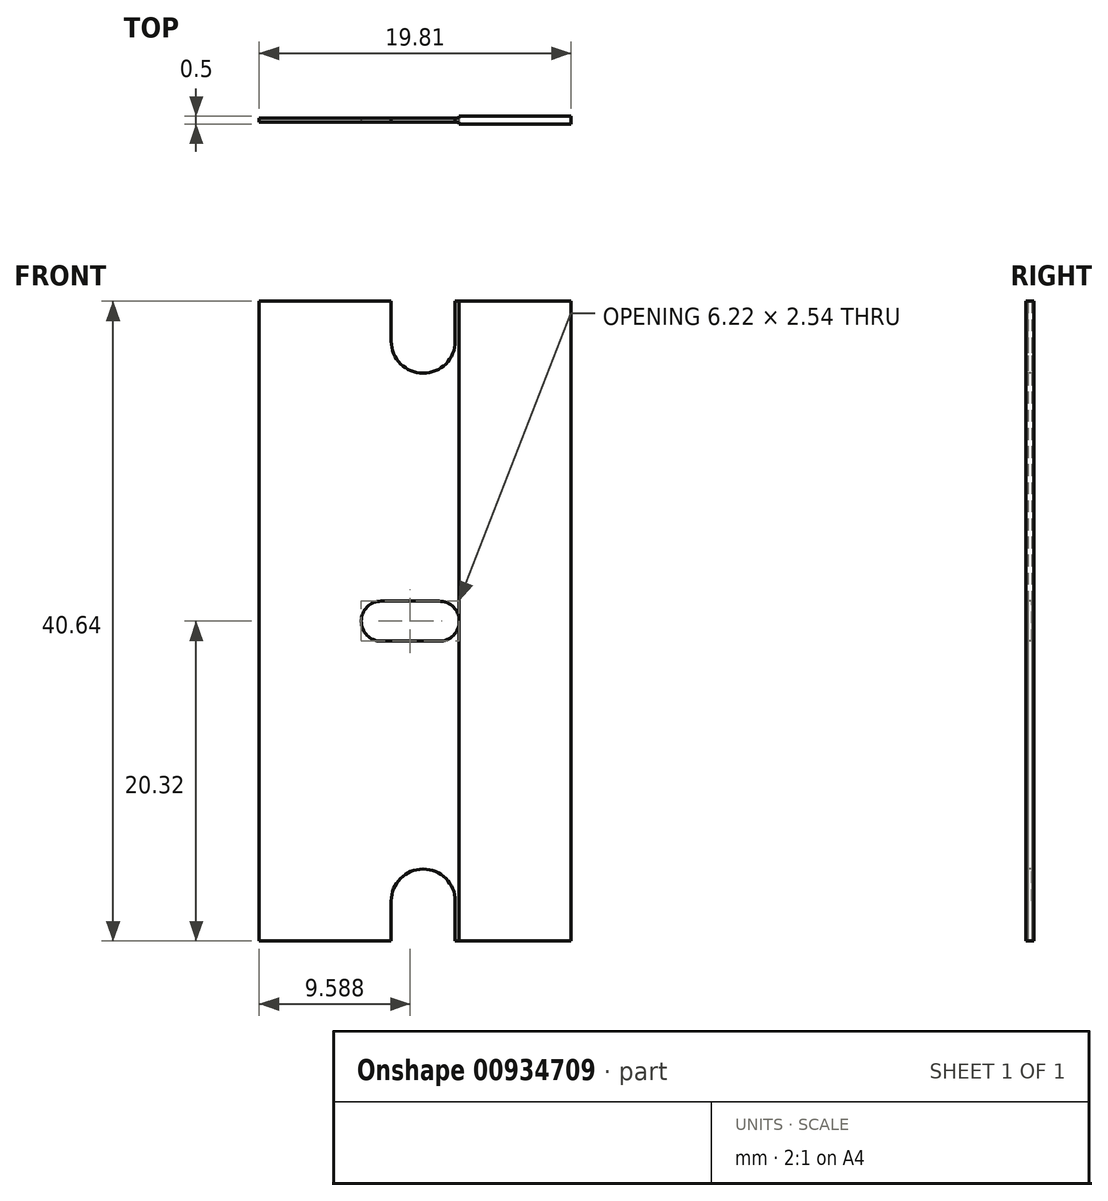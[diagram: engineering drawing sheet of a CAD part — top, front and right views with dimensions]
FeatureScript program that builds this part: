
annotation { "Feature Type Name" : "Feature", "Feature Type Description" : "" }
export const myFeature = defineFeature(function(context is Context, id is Id, definition is map)
    precondition{}
    {
        {
            var Q0;
            Q0=qCreatedBy(makeId("Top.planeOp"),FACE);
            var sketch = newSketch(context, id + "F0", { "sketchPlane" : qUnion([Q0])});
            skLineSegment(sketch, "E0", {"start": v(-12.7, 0.13) * mm, "end": v(0, 0.13) * mm});
            skLineSegment(sketch, "E1", {"start": v(0, 0.13) * mm, "end": v(0, 0.25) * mm});
            skLineSegment(sketch, "E2", {"start": v(0, 0.25) * mm, "end": v(7.11, 0.25) * mm});
            skLineSegment(sketch, "E3", {"start": v(7.11, 0.25) * mm, "end": v(7.11, -0.25) * mm});
            skLineSegment(sketch, "E4", {"start": v(7.11, -0.25) * mm, "end": v(0, -0.25) * mm});
            skLineSegment(sketch, "E5", {"start": v(0, -0.25) * mm, "end": v(0, -0.13) * mm});
            skLineSegment(sketch, "E6", {"start": v(0, -0.13) * mm, "end": v(-12.7, -0.13) * mm});
            skLineSegment(sketch, "E7", {"start": v(-12.7, -0.13) * mm, "end": v(-12.7, 0.13) * mm});
            skLineSegment(sketch, "E8", {"start": v(7.11, 0) * mm, "end": v(-12.7, 0) * mm, "construction": true});
            skSolve(sketch);
        }
        {
            var Q0;
            Q0 = qSketchRegion(id + "F0", true);
            extrude(context, id + "F1", {"entities" : qUnion([Q0]), "depth" : 40.64 * mm, "offsetDistance" : 25.4 * mm});
        }
        {
            var Q0;
            Q0=qCreatedBy(makeId("Front.planeOp"),FACE);
            var sketch = newSketch(context, id + "F2", { "sketchPlane" : qUnion([Q0])});
            skLineSegment(sketch, "E9.left", {"start": v(-4.32, 38.1) * mm, "end": v(-4.32, 40.64) * mm});
            skLineSegment(sketch, "E9.right", {"start": v(-0.25, 38.1) * mm, "end": v(-0.25, 40.64) * mm});
            skLineSegment(sketch, "E10.left", {"start": v(-4.32, 0) * mm, "end": v(-4.32, 2.54) * mm});
            skLineSegment(sketch, "E10.right", {"start": v(-0.25, 0) * mm, "end": v(-0.25, 2.54) * mm});
            skLineSegment(sketch, "E11.bottom", {"start": v(-4.95, 21.6) * mm, "end": v(-1.27, 21.6) * mm});
            skLineSegment(sketch, "E11.top", {"start": v(-4.95, 19.05) * mm, "end": v(-1.27, 19.05) * mm});
            skArc(sketch, "E12", {"start": v(-4.32, 38.1) * mm, "mid": v(-2.29, 36.07) * mm, "end": v(-0.25, 38.1) * mm});
            skArc(sketch, "E13", {"start": v(-4.95, 21.6) * mm, "mid": v(-6.22, 20.32) * mm, "end": v(-4.95, 19.05) * mm});
            skArc(sketch, "E14", {"start": v(-1.27, 21.6) * mm, "mid": v(0, 20.32) * mm, "end": v(-1.27, 19.05) * mm});
            skLineSegment(sketch, "E15", {"start": v(-4.32, 0) * mm, "end": v(-0.25, 0) * mm});
            skLineSegment(sketch, "E16", {"start": v(-4.32, 40.64) * mm, "end": v(-0.25, 40.64) * mm});
            skLineSegment(sketch, "E17", {"start": v(-13.98, 20.32) * mm, "end": v(0, 20.32) * mm, "construction": true});
            skArc(sketch, "E18", {"start": v(-4.32, 2.54) * mm, "mid": v(-2.29, 4.57) * mm, "end": v(-0.25, 2.54) * mm});
            skSolve(sketch);
        }
        {
            var Q0;
            Q0 = qSketchRegion(id + "F2", true);
            extrude(context, id + "F3", {"entities" : qUnion([Q0]), "operationType" : NewBodyOperationType.REMOVE, "endBound" : BoundingType.THROUGH_ALL, "oppositeDirection" : true, "depth" : 25.4 * mm, "offsetDistance" : 25.4 * mm, "hasSecondDirection" : true, "secondDirectionBound" : SecondDirectionBoundingType.THROUGH_ALL, "secondDirectionOppositeDirection" : false, "secondDirectionDepth" : 25.4 * mm});
        }
    });
